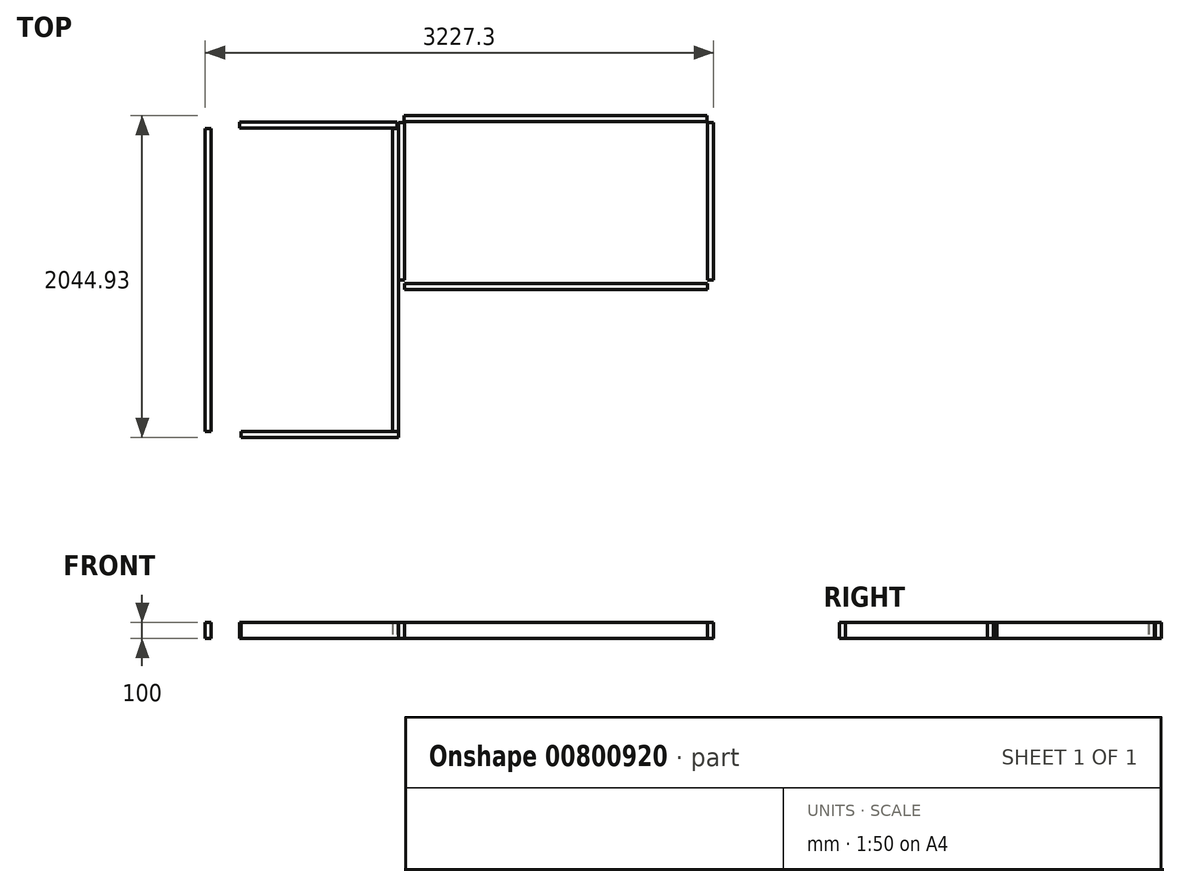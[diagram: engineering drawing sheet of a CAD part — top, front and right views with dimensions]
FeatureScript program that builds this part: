
annotation { "Feature Type Name" : "Feature", "Feature Type Description" : "" }
export const myFeature = defineFeature(function(context is Context, id is Id, definition is map)
    precondition{}
    {
        {
            var Q0;
            Q0=qCreatedBy(makeId("Top.planeOp"),FACE);
            var sketch = newSketch(context, id + "F0", { "sketchPlane" : qUnion([Q0])});
            skPoint(sketch, "E0.middle", {"position": v(0, 0) * mm});
            skLineSegment(sketch, "E1.bottom", {"start": v(1497.3, 1044.3) * mm, "end": v(-426.7, 1044.3) * mm});
            skLineSegment(sketch, "E1.top", {"start": v(1497.3, 1006.3) * mm, "end": v(-426.7, 1006.3) * mm});
            skLineSegment(sketch, "E1.right", {"start": v(-424, 1000) * mm, "end": v(-424, 962) * mm});
            skLineSegment(sketch, "E2.left", {"start": v(-426.7, 1006.3) * mm, "end": v(-426.7, 1044.3) * mm});
            skLineSegment(sketch, "E3.bottom", {"start": v(-1650.89, -961.49) * mm, "end": v(-1650.89, 962.51) * mm});
            skLineSegment(sketch, "E3.top", {"start": v(-1688.89, -961.49) * mm, "end": v(-1688.89, 962.51) * mm});
            skLineSegment(sketch, "E4.bottom", {"start": v(-1471.89, 1004.51) * mm, "end": v(-471.89, 1004.51) * mm});
            skLineSegment(sketch, "E4.top", {"start": v(-1471.89, 966.51) * mm, "end": v(-471.89, 966.51) * mm});
            skLineSegment(sketch, "E4.right", {"start": v(-471.89, 1004.51) * mm, "end": v(-471.89, 966.51) * mm});
            skLineSegment(sketch, "E5.bottom", {"start": v(1538.4, 1000.45) * mm, "end": v(1538.4, 0.45) * mm});
            skLineSegment(sketch, "E6.bottom", {"start": v(-424.67, 1000) * mm, "end": v(-424.67, 0) * mm});
            skLineSegment(sketch, "E6.top", {"start": v(-462.67, 1000) * mm, "end": v(-462.67, 0) * mm});
            skLineSegment(sketch, "E7.bottom", {"start": v(-463, -961.49) * mm, "end": v(-463, 962.51) * mm});
            skLineSegment(sketch, "E7.top", {"start": v(-501, -961.49) * mm, "end": v(-501, 962.51) * mm});
            skLineSegment(sketch, "E8", {"start": v(-501, 962.51) * mm, "end": v(-463, 962.51) * mm});
            skLineSegment(sketch, "E9", {"start": v(-501, -961.49) * mm, "end": v(-463, -961.49) * mm});
            skLineSegment(sketch, "E10", {"start": v(-462.67, 0) * mm, "end": v(-424.67, 0) * mm});
            skLineSegment(sketch, "E11", {"start": v(-424.67, 1000) * mm, "end": v(-462.67, 1000) * mm});
            skLineSegment(sketch, "E12", {"start": v(-1688.89, 962.51) * mm, "end": v(-1650.89, 962.51) * mm});
            skLineSegment(sketch, "E13", {"start": v(-1688.89, -961.49) * mm, "end": v(-1650.89, -961.49) * mm});
            skLineSegment(sketch, "E14", {"start": v(1500, 0.45) * mm, "end": v(1538.4, 0.45) * mm});
            skLineSegment(sketch, "E15.bottom", {"start": v(-1461.98, -962.63) * mm, "end": v(-461.98, -962.63) * mm});
            skLineSegment(sketch, "E15.top", {"start": v(-1461.98, -1000.63) * mm, "end": v(-461.98, -1000.63) * mm});
            skLineSegment(sketch, "E15.left", {"start": v(-1461.98, -962.63) * mm, "end": v(-1461.98, -1000.63) * mm});
            skLineSegment(sketch, "E15.right", {"start": v(-461.98, -962.63) * mm, "end": v(-461.98, -1000.63) * mm});
            skLineSegment(sketch, "E16.bottom", {"start": v(1499.33, -21.4) * mm, "end": v(-424.67, -21.4) * mm});
            skLineSegment(sketch, "E16.top", {"start": v(1499.33, -59.4) * mm, "end": v(-424.67, -59.4) * mm});
            skLineSegment(sketch, "E16.left", {"start": v(1499.33, -21.4) * mm, "end": v(1499.33, -59.4) * mm});
            skLineSegment(sketch, "E17.left", {"start": v(-424.67, -59.4) * mm, "end": v(-424.67, -21.4) * mm});
            skLineSegment(sketch, "E18", {"start": v(1500, 1000) * mm, "end": v(1538.4, 1000.45) * mm});
            skLineSegment(sketch, "E19", {"start": v(-1471.89, 1004.51) * mm, "end": v(-1471.89, 966.51) * mm});
            skLineSegment(sketch, "E20", {"start": v(1497.3, 1044.3) * mm, "end": v(1497.3, 1006.3) * mm});
            skLineSegment(sketch, "E21", {"start": v(1500, 1000) * mm, "end": v(1500, 0.45) * mm});
            skSolve(sketch);
        }
        {
            var Q0;
            Q0 = qSketchRegion(id + "F0", true);
            extrude(context, id + "F1", {"entities" : qUnion([Q0]), "depth" : 100 * mm, "offsetDistance" : 25 * mm});
        }
        {
            var Q0;
            Q0=makeQuery(id+"F1.opExtrude","SWEPT_BODY",BODY,{"disambiguationData":[OSD([sQuery(id+"F0.wireOp",EDGE,"E1.bottom"),sQuery(id+"F0.wireOp",EDGE,"E1.top"),sQuery(id+"F0.wireOp",EDGE,"E2.left"),sQuery(id+"F0.wireOp",EDGE,"E20")])]});
            transform(context, id + "F2", {"entities" : qUnion([Q0]), "transformType" : TransformType.TRANSLATION_3D, "dx" : 0 * mm, "dy" : 0 * mm, "dz" : 0 * mm, "makeCopy" : true});
        }
    });
